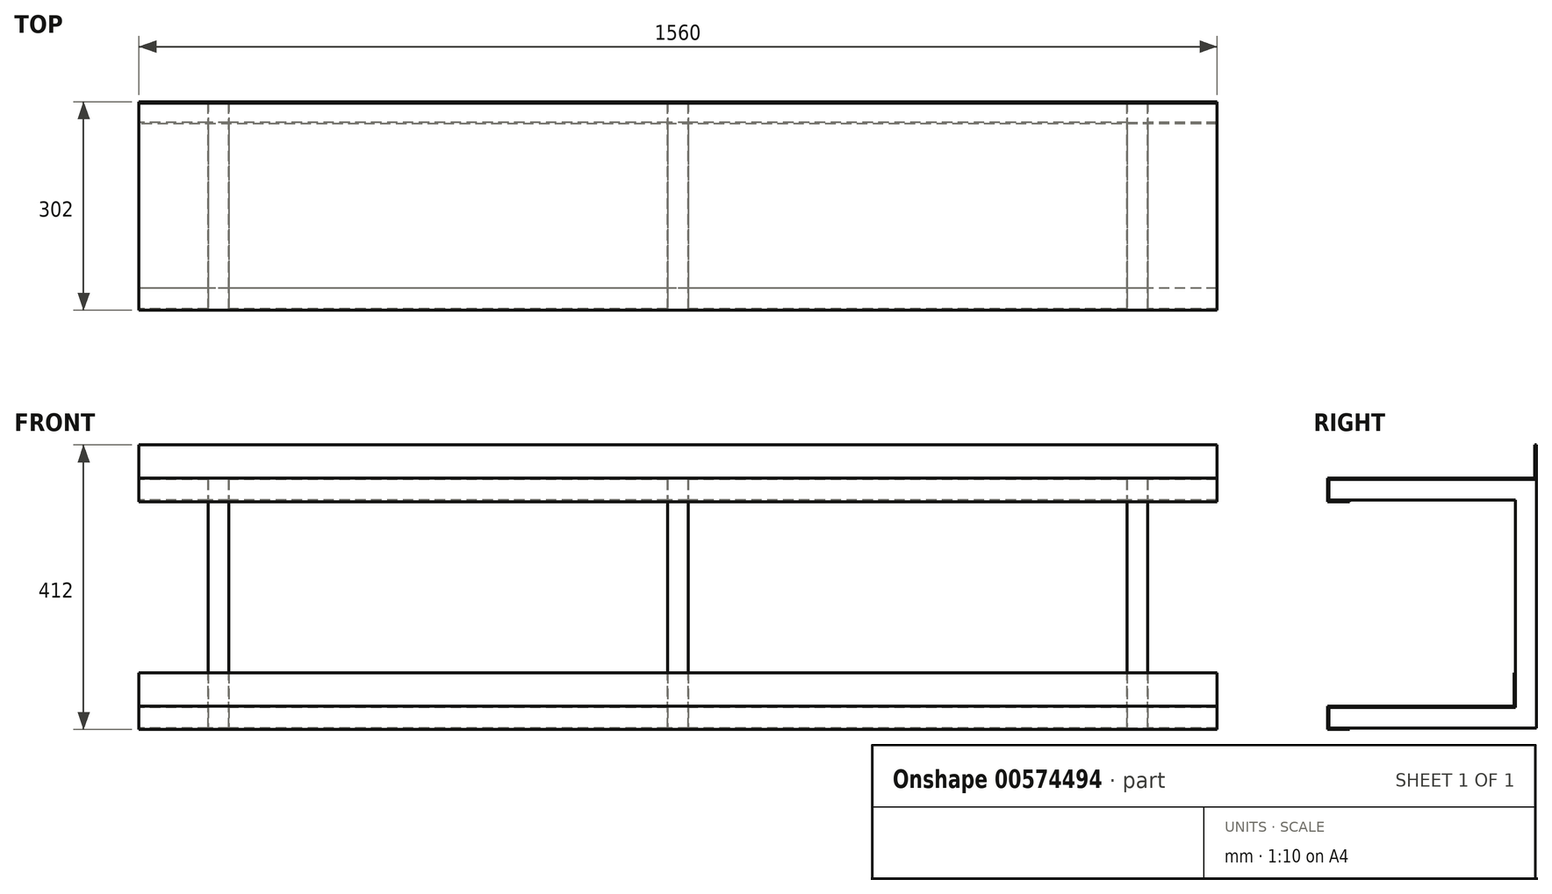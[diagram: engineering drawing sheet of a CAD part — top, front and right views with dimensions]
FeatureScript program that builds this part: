
annotation { "Feature Type Name" : "Feature", "Feature Type Description" : "" }
export const myFeature = defineFeature(function(context is Context, id is Id, definition is map)
    precondition{}
    {
        {
            var Q0;
            Q0=qCreatedBy(makeId("Right.planeOp"),FACE);
            var sketch = newSketch(context, id + "F0", { "sketchPlane" : qUnion([Q0])});
            skLineSegment(sketch, "E0", {"start": v(0, 0) * mm, "end": v(300, 0) * mm});
            skLineSegment(sketch, "E1", {"start": v(300, 0) * mm, "end": v(300, 360) * mm});
            skLineSegment(sketch, "E2", {"start": v(300, 360) * mm, "end": v(0, 360) * mm});
            skLineSegment(sketch, "E3", {"start": v(0, 360) * mm, "end": v(0, 330) * mm});
            skLineSegment(sketch, "E4", {"start": v(0, 330) * mm, "end": v(270, 330) * mm});
            skLineSegment(sketch, "E5", {"start": v(270, 330) * mm, "end": v(270, 30) * mm});
            skLineSegment(sketch, "E6", {"start": v(270, 30) * mm, "end": v(0, 30) * mm});
            skLineSegment(sketch, "E7", {"start": v(0, 30) * mm, "end": v(0, 0) * mm});
            skSolve(sketch);
        }
        {
            var Q0;
            Q0 = qSketchRegion(id + "F0", true);
            extrude(context, id + "F1", {"entities" : qUnion([Q0]), "depth" : 30 * mm, "offsetDistance" : 25 * mm});
        }
        {
            var Q0;
            Q0=qCreatedBy(makeId("Right.planeOp"),FACE);
            cPlane(context, id + "F2", {"entities" : qUnion([Q0]), "cplaneType" : CPlaneType.OFFSET, "offset" : (1560 - 200) * mm, "width" : 150 * mm, "height" : 150 * mm});
        }
        {
            var Q0;
            Q0=qCreatedBy(makeId("Right.planeOp"),FACE);
            var Q1;
            Q1=qCreatedBy(id+"F2.planeOp",FACE);
            cPlane(context, id + "F3", {"entities" : qUnion([Q0, Q1]), "cplaneType" : CPlaneType.MID_PLANE, "offset" : 25 * mm, "width" : 150 * mm, "height" : 150 * mm});
        }
        {
            var Q0;
            Q0=qCreatedBy(id+"F2.planeOp",FACE);
            var sketch = newSketch(context, id + "F4", { "sketchPlane" : qUnion([Q0])});
            skLineSegment(sketch, "E8", {"start": v(0, 0) * mm, "end": v(300, 0) * mm});
            skLineSegment(sketch, "E9", {"start": v(300, 0) * mm, "end": v(300, 360) * mm});
            skLineSegment(sketch, "E10", {"start": v(300, 360) * mm, "end": v(0, 360) * mm});
            skLineSegment(sketch, "E11", {"start": v(0, 360) * mm, "end": v(0, 330) * mm});
            skLineSegment(sketch, "E12", {"start": v(0, 330) * mm, "end": v(270, 330) * mm});
            skLineSegment(sketch, "E13", {"start": v(270, 330) * mm, "end": v(270, 30) * mm});
            skLineSegment(sketch, "E14", {"start": v(270, 30) * mm, "end": v(0, 30) * mm});
            skLineSegment(sketch, "E15", {"start": v(0, 30) * mm, "end": v(0, 0) * mm});
            skSolve(sketch);
        }
        {
            var Q0;
            Q0 = qSketchRegion(id + "F4", true);
            extrude(context, id + "F5", {"entities" : qUnion([Q0]), "oppositeDirection" : true, "depth" : 30 * mm, "offsetDistance" : 25 * mm});
        }
        {
            var Q0;
            Q0=qCreatedBy(id+"F3.planeOp",FACE);
            var sketch = newSketch(context, id + "F6", { "sketchPlane" : qUnion([Q0])});
            skLineSegment(sketch, "E16", {"start": v(0, 0) * mm, "end": v(300, 0) * mm});
            skLineSegment(sketch, "E17", {"start": v(300, 0) * mm, "end": v(300, 360) * mm});
            skLineSegment(sketch, "E18", {"start": v(300, 360) * mm, "end": v(0, 360) * mm});
            skLineSegment(sketch, "E19", {"start": v(0, 360) * mm, "end": v(0, 330) * mm});
            skLineSegment(sketch, "E20", {"start": v(0, 330) * mm, "end": v(270, 330) * mm});
            skLineSegment(sketch, "E21", {"start": v(270, 330) * mm, "end": v(270, 30) * mm});
            skLineSegment(sketch, "E22", {"start": v(270, 30) * mm, "end": v(0, 30) * mm});
            skLineSegment(sketch, "E23", {"start": v(0, 30) * mm, "end": v(0, 0) * mm});
            skSolve(sketch);
        }
        {
            var Q0;
            Q0 = qSketchRegion(id + "F6", true);
            extrude(context, id + "F7", {"entities" : qUnion([Q0]), "depth" : 15 * mm, "offsetDistance" : 25 * mm, "hasSecondDirection" : true, "secondDirectionOppositeDirection" : true, "secondDirectionDepth" : 15 * mm});
        }
        {
            var Q0;
            Q0=qCreatedBy(id+"F3.planeOp",FACE);
            var sketch = newSketch(context, id + "F8", { "sketchPlane" : qUnion([Q0])});
            skLineSegment(sketch, "E24", {"start": v(0, 0) * mm, "end": v(0, 30) * mm});
            skLineSegment(sketch, "E25", {"start": v(0, 30) * mm, "end": v(270, 30) * mm});
            skLineSegment(sketch, "E26", {"start": v(270, 30) * mm, "end": v(270, 80) * mm});
            skLineSegment(sketch, "E27", {"start": v(270, 80) * mm, "end": v(268, 80) * mm});
            skLineSegment(sketch, "E28", {"start": v(268, 80) * mm, "end": v(268, 32) * mm});
            skLineSegment(sketch, "E29", {"start": v(268, 32) * mm, "end": v(-2, 32) * mm});
            skLineSegment(sketch, "E30", {"start": v(0, 30) * mm, "end": v(0, 0) * mm});
            skLineSegment(sketch, "E31", {"start": v(0, 0) * mm, "end": v(0, 0) * mm});
            skLineSegment(sketch, "E32", {"start": v(0, 330) * mm, "end": v(0, 360) * mm});
            skLineSegment(sketch, "E33", {"start": v(0, 360) * mm, "end": v(300, 360) * mm});
            skLineSegment(sketch, "E34", {"start": v(300, 360) * mm, "end": v(300, 410) * mm});
            skLineSegment(sketch, "E35", {"start": v(300, 410) * mm, "end": v(298, 410) * mm});
            skLineSegment(sketch, "E36", {"start": v(298, 410) * mm, "end": v(298, 362) * mm});
            skLineSegment(sketch, "E37", {"start": v(298, 362) * mm, "end": v(-2, 362) * mm});
            skLineSegment(sketch, "E38", {"start": v(-2, 362) * mm, "end": v(-2, 328) * mm});
            skLineSegment(sketch, "E39", {"start": v(-2, -2) * mm, "end": v(-2, 32) * mm});
            skPoint(sketch, "E40.orphan", {"position": v(0, 32) * mm});
            skLineSegment(sketch, "E41", {"start": v(0, 0) * mm, "end": v(30, 0) * mm});
            skLineSegment(sketch, "E42", {"start": v(30, 0) * mm, "end": v(30, -2) * mm});
            skLineSegment(sketch, "E43", {"start": v(30, -2) * mm, "end": v(-2, -2) * mm});
            skPoint(sketch, "E44.orphan", {"position": v(-2, 0) * mm});
            skLineSegment(sketch, "E45", {"start": v(0, 330) * mm, "end": v(30, 330) * mm});
            skLineSegment(sketch, "E46", {"start": v(30, 330) * mm, "end": v(30, 328) * mm});
            skLineSegment(sketch, "E47", {"start": v(30, 328) * mm, "end": v(-2, 328) * mm});
            skPoint(sketch, "E48.orphan", {"position": v(-2, 330) * mm});
            skSolve(sketch);
        }
        {
            var Q0;
            Q0 = qSketchRegion(id + "F8", true);
            extrude(context, id + "F9", {"entities" : qUnion([Q0]), "operationType" : NewBodyOperationType.ADD, "depth" : 780 * mm, "offsetDistance" : 25 * mm, "hasSecondDirection" : true, "secondDirectionOppositeDirection" : true, "secondDirectionDepth" : 780 * mm});
        }
    });
